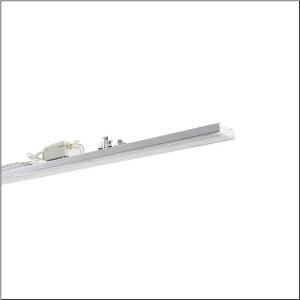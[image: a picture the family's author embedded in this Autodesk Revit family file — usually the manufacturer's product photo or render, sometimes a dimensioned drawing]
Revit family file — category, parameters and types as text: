
# Revit family: licross_r__21_recessed_mo_52te10cn49xg_034d
name_source: partatom
category: Lighting Fixtures
units: mm (PartAtom-declared; Revit-internal decimal feet)

## family parameters
Cut with Voids When Loaded = No
Host = Face
Light Source = No
Part Type = Normal
Room Calculation Point = No
Round Connector Dimension = Use Diameter
Shared = No

## types (1)
- --- (1 x LED, 9010 lm, 49.9 W, 4000K)
    Apparent Load = 50 VA
    CIE Flux Codes = 50 81 96 100 100
    Color Rendering = 80
    Color Temperature = 4000K
    Default Elevation = 1800 mm
    Description = Licross® 21 Recessed MO, luminaire insert, of sheet steel, galvanised, coil coated, white, length: 1.500mm, width: 66mm, height: 67mm, LED rated luminous flux: 9.010lm, light colour: 840, control gear: ON/OFF Multilumen, CLOi, control gear: ECG Multilumen, with plug, 3-pole, with phase selection, mains connection: 220..240V, AC, 50/60Hz, start of lifetime: 49W, end of service life: 61W, halogen-free wiring, primary optical cover: cover, of PMMA, light emission: direct distribution, primary light characteristic: symmetric, protection rating (complete): IP54, insulation class (complete): insulation class I (protective earthing), certification: CE, ENEC, VDE, UKCA, protection symbol: D if used in an environment with non-conductive dust loads with corresponding accessories, impact resistance: IK06, permissible ambient temperature for indoor applications: -35..+40°C, corresponds to IFS (International Featured Standards) requirements for safety and quality in the food industry, reducing of maximum allowable ambient temperature of 5°C with ceiling mounting, LABS conformity tested according to VDMA 24364:2018-05, packaging unit: 1 piece
    Height = 58 mm
    Lamp = 1 x LED
    Lamp Light Flux = 9010 lm
    Lamp Power = 49.9 W
    Lamp count = 1
    Length = 1500 mm
    Luminous efficacy = 181 lm/W
    Manufacturer = Siteco
    ModVariant = No
    Model = 52TE10CN49XG
    Mounting Place = Ceiling
    Mounting Type = Pendant
    Number of Poles = 1
    OnlyDefault = Yes
    Power Factor = 1
    Product Name = Licross® 21 Recessed MO
    Product group = luminaire insert
    ProductGroupID = 901
    Protection Class = Protection class I
    Protection Degree = IP 54
    RLX_Detail_Level = 1
    RLX_Emergency_Light_Flux = 0 lm
    RLX_Emergency_Type = 0
    RLX_Emergency_Type_DB = No
    RlxData = <blob elided: 22133 chars, md5=3e7f62a3>
    Socket = socket
    Standby Power = 0 W
    System Light Flux = 9010 lm
    System Power = 50 W
    Type Comments = factory setting: luminous flux: 100 % | (A | C | E) | 116 mA
    Type Image = l_1296930.jpg
    URL = http://relux.com
    VarID = @adj_040817
    Voltage = 0 V
    Weight = 0.00 kg
    Width = 66 mm

## geometry (parser evidence)
native form markers: Blend x4, Sweep x13
no freeform markers — native parametric forms only
